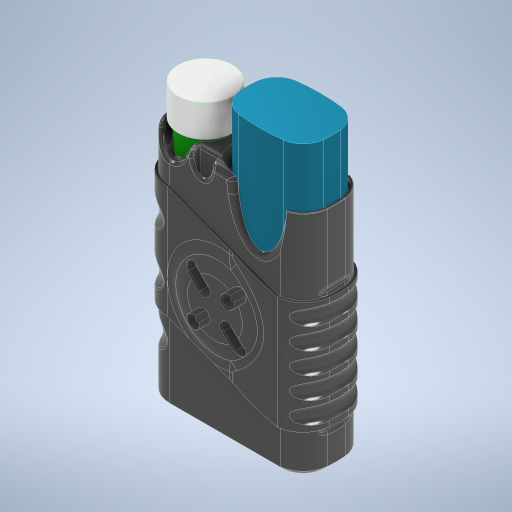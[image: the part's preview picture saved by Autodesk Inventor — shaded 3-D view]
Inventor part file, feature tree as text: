
AUTODESK INVENTOR PART (.ipt)
format: ipt  version: 2024.1 (Build 281209000, 209)  size: 3,731,456 bytes
history: native  units: mm
features: fillet x35, projected_geometry x33, extrude x26, sketch x14, other x6, revolve x6, sweep x2, pattern_circular x2, chamfer x2, plane x1, mirror x1
ambient origin geometry x8: Origin, YZ Plane, XZ Plane, XY Plane, X Axis, Y Axis, Z Axis, Center Point
bodies: Body1 (feature_tree), Body2 (feature_tree), Body3 (feature_tree), Body4 (feature_tree)
feature tree (128):
  other  "vape"
  extrude  "Extrusion1"  Depth=8.35mm
  fillet  "Fillet1"  Radius=80.0mm
  extrude  "Extrusion2"  Depth=11.6mm TaperAngle=0.0deg
  plane  "Work Plane1"
  extrude  "Extrusion3"  Depth=45.8mm TaperAngle=0.0deg
  extrude  "Extrusion4"  Depth=22.1mm
  extrude  "Extrusion5"  Depth=1.5mm
  extrude  "Extrusion6"  Depth=1.5mm
  fillet  "Fillet2"  Radius=1.5mm
  extrude  "Extrusion8"  Depth=15.55mm
  extrude  "Extrusion20"  Depth=3.0mm
  extrude  "Extrusion21"  Depth=3.0mm
  sweep  "Sweep2"
  extrude  "Extrusion22"  Depth=13.0mm
  fillet  "Fillet22"  Radius=2.0mm
  fillet  "Fillet23"  Radius=10.0mm
  fillet  "Fillet24"  Radius=11.0mm
  fillet  "Fillet25"  Radius=6.0mm
  fillet  "Fillet26"  Radius=2.0mm
  fillet  "Fillet4"  Radius=3.0mm
  extrude  "Extrusion10"  Depth=2.4mm
  extrude  "Extrusion11"  Depth=7.3mm
  fillet  "Fillet10"  Radius=7.0mm
  fillet  "Fillet27"  Radius=45.0mm
  extrude  "Extrusion13"  Depth=0.25mm
  fillet  "Fillet28"  Radius=71.0mm
  extrude  "vapeLID"  Depth=71.0mm TaperAngle=0.0deg
  extrude  "Extrusion15"  Depth=3.0mm TaperAngle=30.0deg
  fillet  "Fillet29"  Radius=1.0mm
  extrude  "Extrusion25"  Depth=15.0mm TaperAngle=0.0deg
  fillet  "Fillet30"  Radius=15.0mm
  other  "Work Axis1"
  sketch  "Sketch29"  dims[d28=17.0mm d29=45.8mm d30=0.0mm]
  revolve  "Revolution1"  [1 undecoded]
  sketch  "Sketch30"  dims[d31=17.0mm d38=22.1mm]
  revolve  "Revolution2"  [1 undecoded]
  fillet  "Fillet32"  Radius=15.0mm
  extrude  "Extrusion26"  Depth=15.780931mm
  revolve  "Revolution3"  [1 undecoded]
  revolve  "Revolution5"  [1 undecoded]
  extrude  "Extrusion27"  Depth=7.5mm
  extrude  "Extrusion28"  Depth=6.0mm
  fillet  "Fillet34"  Radius=3.0mm
  other  "Work Axis2"
  revolve  "Revolution6"  [1 undecoded]
  pattern_circular  "Circular Pattern1"  [2 undecoded]
  extrude  "Extrusion29"  Depth=1.0mm
  fillet  "Fillet35"  Radius=0.5mm
  fillet  "Fillet36"  Radius=1.0mm
  fillet  "Fillet37"  Radius=24.0mm
  fillet  "Fillet38"  Radius=2.5mm
  fillet  "Fillet39"  Radius=0.7mm
  fillet  "Fillet40"  Radius=3.0mm
  fillet  "Fillet41"  Radius=5.0mm
  pattern_circular  "Circular Pattern2"  [2 undecoded]
  fillet  "Fillet42"  Radius=1.5mm
  fillet  "Fillet43"  Radius=6.0mm
  fillet  "Fillet45"  Radius=3.65mm
  fillet  "Fillet46"  Radius=10.0mm
  extrude  "Extrusion30"  Depth=1.5mm
  extrude  "Extrusion35"  Depth=14.0mm
  fillet  "Fillet53"  Radius=19.0mm
  fillet  "Fillet54"  [1 undecoded]
  fillet  "Fillet55"  Radius=7.8mm
  chamfer  "Chamfer2"  Distance=8.0mm
  mirror  "Mirror1"
  fillet  "Fillet56"  Radius=7.8mm
  fillet  "Fillet57"  Radius=7.8mm
  extrude  "Extrusion31"  Depth=7.8mm
  extrude  "Extrusion32"  TaperAngle=0.0deg  [1 undecoded]
  sketch  "Sketch48"  dims[d48=3.0mm d49=3.0mm]
  sweep  "Sweep3"
  revolve  "Revolution8"  [1 undecoded]
  fillet  "Fillet48"  Radius=18.25mm
  chamfer  "Chamfer3"  Distance=6.0mm
  extrude  "Extrusion33"  Depth=6.0mm
  extrude  "Extrusion34"  Depth=6.0mm
  fillet  "Fillet49"  [1 undecoded]
  fillet  "Fillet50"  Radius=3.0mm
  fillet  "Fillet51"  Radius=6.0mm
  other  "vape-tube"
  other  "storage"
  projected_geometry  "Projected Loop2"
  projected_geometry  "Projected Loop3"
  projected_geometry  "Projected Loop4"
  projected_geometry  "Projected Loop6"
  other  "vape-lid"
  projected_geometry  "Projected Loop13"
  sketch  "Sketch23"  dims[d4=98.5mm d5=0.0mm d9=8.35mm d22=80.0mm d23=0.0mm]
  projected_geometry  "Projected Loop14"
  sketch  "Sketch25"  dims[d24=20.0mm d26=11.6mm d27=0.0mm]
  projected_geometry  "Projected Loop15"
  sketch  "Sketch37"  dims[d39=31.1mm d41=1.5mm]
  projected_geometry  "Projected Loop32"
  projected_geometry  "Projected Loop33"
  projected_geometry  "Projected Loop34"
  projected_geometry  "Projected Loop35"
  sketch  "Sketch45"  dims[d42=1.5mm d44=1.5mm d45=1.5mm]
  projected_geometry  "Projected Loop36"
  projected_geometry  "Projected Loop37"
  projected_geometry  "Projected Loop38"
  projected_geometry  "Projected Loop39"
  sketch  "Sketch47"  dims[d46=11.05mm d47=15.55mm]
  sketch  "Sketch49"  dims[d50=3.0mm d51=3.0mm]
  sketch  "3D Sketch1"
  sketch  "Sketch51"  dims[d52=11.05mm d53=15.55mm]
  sketch  "Sketch52"  dims[d54=2.5mm d55=13.0mm]
  projected_geometry  "Projected Loop53"
  sketch  "Sketch53"  dims[d56=12.5mm d57=60.0mm d58=0.0mm d59=2.0mm d60=10.0mm d61=0.0mm d62=11.0mm d66=6.0mm d67=0.0mm d69=2.0mm d83=3.0mm]
  projected_geometry  "Projected Loop60"
  projected_geometry  "Projected Loop61"
  projected_geometry  "Projected Loop62"
  projected_geometry  "Projected Loop63"
  projected_geometry  "Projected Loop64"
  projected_geometry  "Projected Loop65"
  projected_geometry  "Projected Loop66"
  projected_geometry  "Projected Loop67"
  projected_geometry  "Projected Loop68"
  projected_geometry  "Projected Loop69"
  projected_geometry  "Projected Loop70"
  projected_geometry  "Projected Loop71"
  projected_geometry  "Projected Loop72"
  sketch  "Sketch54"  dims[d86=72.0mm d87=0.0mm d88=2.4mm d89=7.3mm d91=7.0mm d92=45.0mm d93=0.0mm d94=0.25mm d105=71.0mm d106=0.0mm d108=71.0mm d109=0.0mm d110=3.0mm d111=30.0deg d158=1.0mm d159=15.0mm d160=0.0mm d161=15.0mm d162=0.0mm d163=0.0mm d164=0.0mm d169=0.0mm d170=0.0mm d171=15.0mm d172=15.780931mm d173=20.0mm d174=9.0mm d175=7.5mm d176=6.0mm d177=3.0mm d178=1.0mm d179=2.0mm d180=1.0mm d181=0.5mm d182=1.0mm d183=24.0mm d184=2.5mm d185=0.7mm d186=3.0mm d187=5.0mm d188=0.5mm d193=1.5mm d194=6.0mm d195=3.65mm d196=10.0mm d197=0.0mm d198=1.5mm d199=14.0mm d200=19.0mm d201=19.0mm d207=180.0deg d208=7.8mm d209=8.0mm d210=7.8mm d211=7.8mm d212=7.8mm d215=0.0mm d216=180.0deg d218=1.5mm d221=18.25mm d222=0.0mm d225=6.0mm d226=6.0mm d229=6.0mm d230=180.0deg d240=3.0mm d241=6.0mm d242=6.0mm d243=6.0mm d245=12.0mm d247=180.0deg d249=20.0mm d253=22.0mm d254=22.0mm d255=25.0mm d256=1.0mm d257=1.0mm d258=0.0mm d259=1.0mm d260=0.0mm d261=0.2mm d263=5.0mm d264=10.0mm d266=10.0mm d267=30.0mm d268=4.0mm d269=45.0deg d270=40.0mm d271=360.0deg d275=0.4mm d276=1.1mm d277=2.4mm d278=3.0mm d279=1.5mm d280=3.0mm d281=0.810487mm d282=2.943591mm d283=4.5mm d284=0.0mm d285=2.0mm d286=0.7mm d287=3.0mm d288=0.5mm d289=1.0mm d290=1.0mm d291=1.0mm d292=40.0mm d293=360.0deg d295=1.0mm d296=0.4mm d298=1.0mm d299=0.4mm d312=12.0mm d315=8.5mm d316=8.5mm d317=5.0mm d318=40.0mm d320=360.0deg d322=10.0mm d323=0.8mm d324=0.0mm d325=0.0mm d329=1.5mm d330=2.0mm d331=45.0deg d332=21.0mm d334=5.458726mm d335=20.0mm d336=30.0mm d337=42.5mm d338=30.0mm d339=0.0mm d340=15.0mm d341=0.0mm d342=0.0mm d343=0.0mm d344=30.754897mm d349=22.0mm d350=24.0mm d351=180.0deg d352=2.0mm d353=2.0mm d354=15.0mm d355=45.0deg d365=1.5mm d366=1.5mm d367=15.0mm d368=0.0mm d369=1.5mm d370=0.25mm d371=0.25mm d372=1.4mm d375=7.5mm d376=0.0mm d377=0.4mm d378=0.4mm d385=25.089685mm d387=0.5mm d388=12.0mm d389=6.0mm d390=6.0mm d391=1.5mm d392=1.5mm d396=0.25mm d397=1.5mm d398=0.25mm d399=1.5mm d400=1.6mm d402=33.5mm d403=1.5mm d404=0.0mm d405=16.0mm d406=11.0mm d407=8.0mm d408=11.5mm d409=8.0mm]
  projected_geometry  "Projected Loop73"
  projected_geometry  "Projected Loop74"
  projected_geometry  "Projected Loop75"
  projected_geometry  "Projected Loop76"
note: 13 required parameter values undecoded (feature->parameter linkage not recoverable at this tier; creation-order binding heuristic only, values carry confidence <= 0.55)